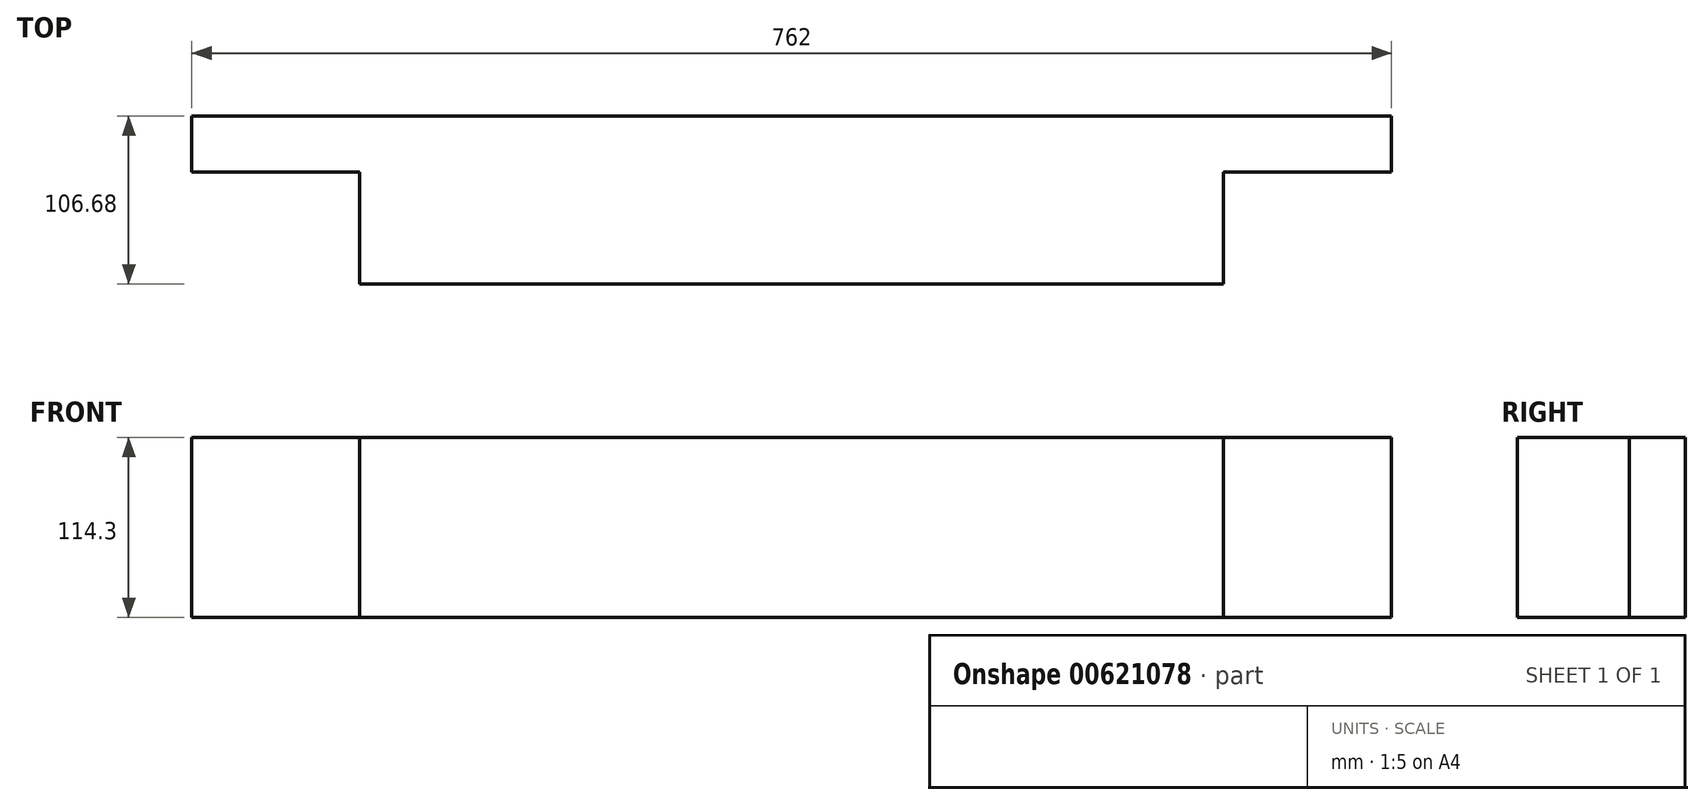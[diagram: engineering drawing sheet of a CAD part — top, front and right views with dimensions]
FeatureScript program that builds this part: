
annotation { "Feature Type Name" : "Feature", "Feature Type Description" : "" }
export const myFeature = defineFeature(function(context is Context, id is Id, definition is map)
    precondition{}
    {
        {
            var Q0;
            Q0=qCreatedBy(makeId("Front.planeOp"),FACE);
            var sketch = newSketch(context, id + "F0", { "sketchPlane" : qUnion([Q0])});
            skLineSegment(sketch, "E0.bottom", {"start": v(-381, 57.15) * mm, "end": v(381, 57.15) * mm});
            skLineSegment(sketch, "E0.top", {"start": v(-381, -57.15) * mm, "end": v(381, -57.15) * mm});
            skLineSegment(sketch, "E0.left", {"start": v(-381, 57.15) * mm, "end": v(-381, -57.15) * mm});
            skLineSegment(sketch, "E0.right", {"start": v(381, 57.15) * mm, "end": v(381, -57.15) * mm});
            skSolve(sketch);
        }
        {
            var Q0;
            Q0=makeQuery(id+"F0.imprint","IMPRINT",FACE,{"disambiguationData":[TD([[makeQuery(id+"F0.imprint","IMPRINT",EDGE,{"derivedFrom":sQuery(id+"F0.wireOp",EDGE,"E0.bottom")}),-1.0]])]});
            extrude(context, id + "F1", {"entities" : qUnion([Q0]), "depth" : 35.56 * mm, "offsetDistance" : 25.4 * mm});
        }
        {
            var Q0;
            Q0=makeQuery(id+"F1.opExtrude","CAP_FACE",FACE,{"disambiguationData":[OSD([sQuery(id+"F0.wireOp",EDGE,"E0.bottom"),sQuery(id+"F0.wireOp",EDGE,"E0.top"),sQuery(id+"F0.wireOp",EDGE,"E0.left"),sQuery(id+"F0.wireOp",EDGE,"E0.right")])],"isStart":false});
            var sketch = newSketch(context, id + "F2", { "sketchPlane" : qUnion([Q0])});
            skLineSegment(sketch, "E1.bottom", {"start": v(-274.32, 57.15) * mm, "end": v(274.32, 57.15) * mm});
            skLineSegment(sketch, "E1.top", {"start": v(-274.32, -57.15) * mm, "end": v(274.32, -57.15) * mm});
            skLineSegment(sketch, "E1.left", {"start": v(-274.32, 57.15) * mm, "end": v(-274.32, -57.15) * mm});
            skLineSegment(sketch, "E1.right", {"start": v(274.32, 57.15) * mm, "end": v(274.32, -57.15) * mm});
            skSolve(sketch);
        }
        {
            var Q0;
            Q0 = qSketchRegion(id + "F2", true);
            extrude(context, id + "F3", {"entities" : qUnion([Q0]), "operationType" : NewBodyOperationType.ADD, "depth" : 71.12 * mm, "offsetDistance" : 25.4 * mm});
        }
    });
